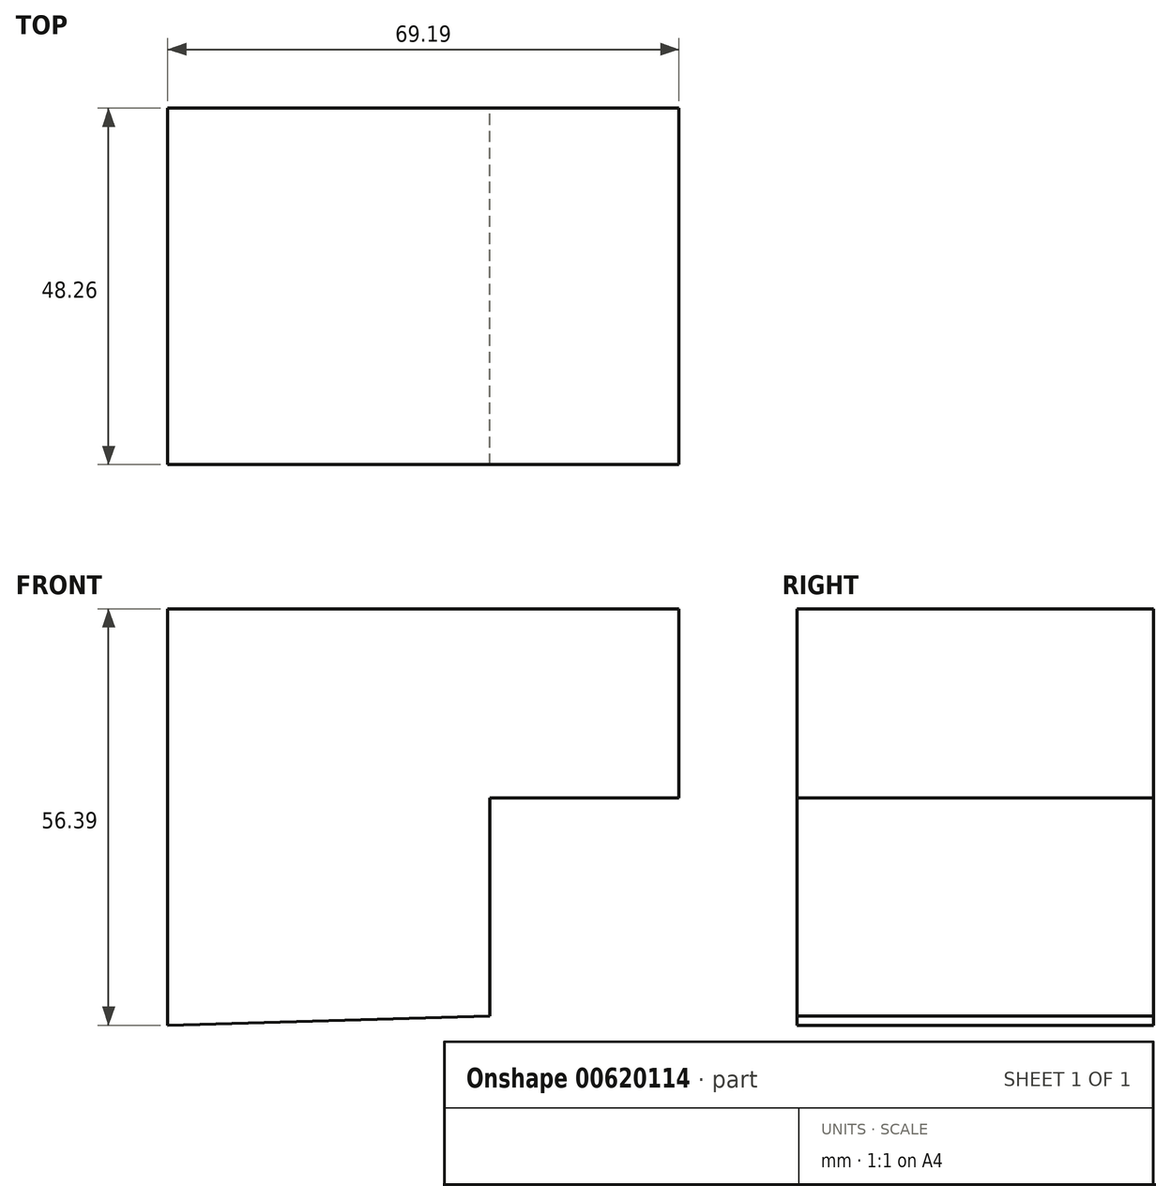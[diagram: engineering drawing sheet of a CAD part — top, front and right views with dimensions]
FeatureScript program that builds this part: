
annotation { "Feature Type Name" : "Feature", "Feature Type Description" : "" }
export const myFeature = defineFeature(function(context is Context, id is Id, definition is map)
    precondition{}
    {
        {
            var Q0;
            Q0=qCreatedBy(makeId("Front.planeOp"),FACE);
            var sketch = newSketch(context, id + "F0", { "sketchPlane" : qUnion([Q0])});
            skLineSegment(sketch, "E0", {"start": v(-33.07, 34.75) * mm, "end": v(36.12, 34.75) * mm});
            skLineSegment(sketch, "E1", {"start": v(36.12, 34.75) * mm, "end": v(36.12, 9.14) * mm});
            skLineSegment(sketch, "E2", {"start": v(36.12, 9.14) * mm, "end": v(10.52, 9.14) * mm});
            skLineSegment(sketch, "E3", {"start": v(10.52, 9.14) * mm, "end": v(10.52, -20.42) * mm});
            skLineSegment(sketch, "E4", {"start": v(-33.07, 34.75) * mm, "end": v(-33.07, -21.64) * mm});
            skLineSegment(sketch, "E5", {"start": v(-33.07, -21.64) * mm, "end": v(10.52, -20.42) * mm});
            skSolve(sketch);
        }
        {
            var Q0;
            Q0 = qSketchRegion(id + "F0", true);
            extrude(context, id + "F1", {"entities" : qUnion([Q0]), "depth" : 48.26 * mm, "offsetDistance" : 25.4 * mm});
        }
    });
